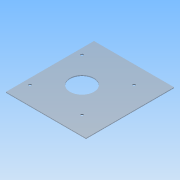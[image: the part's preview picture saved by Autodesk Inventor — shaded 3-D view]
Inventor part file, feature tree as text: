
AUTODESK INVENTOR PART (.ipt)
format: ipt  version: 2016 (Build 200138000, 138)  size: 90,624 bytes
history: native  units: mm
features: sketch x3, hole x2, extrude x1
ambient origin geometry x8: Origin, YZ Plane, XZ Plane, XY Plane, X Axis, Y Axis, Z Axis, Center Point
bodies: Volumenkörper1 (feature_tree)
feature tree (6):
  extrude  "Extrusion1"  Depth=80.0mm
  hole  "Bohrung1"  [1 undecoded]
  hole  "Bohrung2"  [1 undecoded]
  sketch  "Skizze1"  dims[d0=90.0mm d1=80.0mm]
  sketch  "Skizze2"  dims[d2=1.0mm d3=0.0mm]
  sketch  "Skizze3"  dims[d6=30.0mm d7=6.0mm d8=4.0mm d9=2.0mm d10=90.0deg d11=8.0mm d12=20.594885mm d13=40.0mm d14=70.0mm d16=4.5mm d17=6.0mm d18=4.0mm d19=2.0mm d20=90.0deg d21=8.0mm d22=20.594885mm d23=40.0mm]
note: 2 required parameter values undecoded (feature->parameter linkage not recoverable at this tier; creation-order binding heuristic only, values carry confidence <= 0.55)
